# Revit family: Valve_TMV_Emergency-Bradley_Corp-S19-2150-EFX20
name_source: partatom
category: Pipe Accessories
units: mm (PartAtom-declared; Revit-internal decimal feet)

## family parameters
Always vertical = Yes
Cut with Voids When Loaded = No
Part Type = Valve - Breaks Into
Round Connector Dimension = Use Radius
Shared = No
Work Plane-Based = No

## types (1)
- S19-2150 EFX20
    A = 7 "
    ADA Compliant = Yes
    Assembly Code = D2090800
    B = 2 "
    C = 3.25 "
    Cabinet Depth = 6.5 "
    Cabinet Flange Height = 26 "
    Cabinet Flange Width = 26 "
    Cabinet Height = 24 "
    Cabinet Material = Metal - Bradley Corp - Stainless Steel
    Cabinet Width = 24 "
    Cabinet Window Material = Plastic - Bradley Corp - Plexi-glass
    D = 4.75 "
    Default Elevation = 0 "
    Description = Emergency TMV Thermostatic Mixing Valve EFX20 with Optional Cabinet
    E = 8 "
    F = 14 "
    G = 3.125 "
    H = 9.25 "
    Industry Standards = ASSE 1017, UPC & CSA. Certified by IAPMO to meet the lead-free requirements of CA AB 1953.
    Manufacturer = Bradley Corporation
    Manufacturer Installation URL - English = https://www.bradleycorp.com
    MasterFormat Number = 22 40 00
    MasterFormat Title = Plumbing Fixtures
    Material = Lead-free Brass
    Maximum Inlet Temperature = 200°F (93°C)
    Maximum Operating Pressure = 125.00 psi
    Minimum Flow = 3 GPM
    Model = S19-2150 EFX20
    Nut Material = Metal - Bradley Corp - Light Bronze
    OmniClass Code = 23.65.55.14.24
    OmniClass Title = Mixing Valves for Liquid Services
    Percentage of Recycled Content = 0
    Product Page URL = https://www.bradleycorp.com
    Product Tech Data URL - English = https://www.bradleycorp.com
    Set Point = 110°F (43°C)
    Set Point Notes = "Refer to Bradley Technical Data for other set points. "
    Specifications URL = http://www.bradleycorp.com
    Temperature Notes = "Refer to Bradley Technical Data for other temperature ranges."
    Temperature Range = Std. 90°F (32°C) to 120°F (49°C)
    Top Nut Placement 2 = 1.417 "
    URL = http://www.bradleycorp.com
    Valve Material = Metal - Bradley Corp - Bronze
    Version = 1.0
    XRadius = 0"
    Xnpt = 1"
    YRadius = 1"
    Ynpt = 1"
    ZRadius = 0"
    Znpt = 1"

## geometry (parser evidence)
native form markers: Blend x10, Sweep x3
no freeform markers — native parametric forms only
